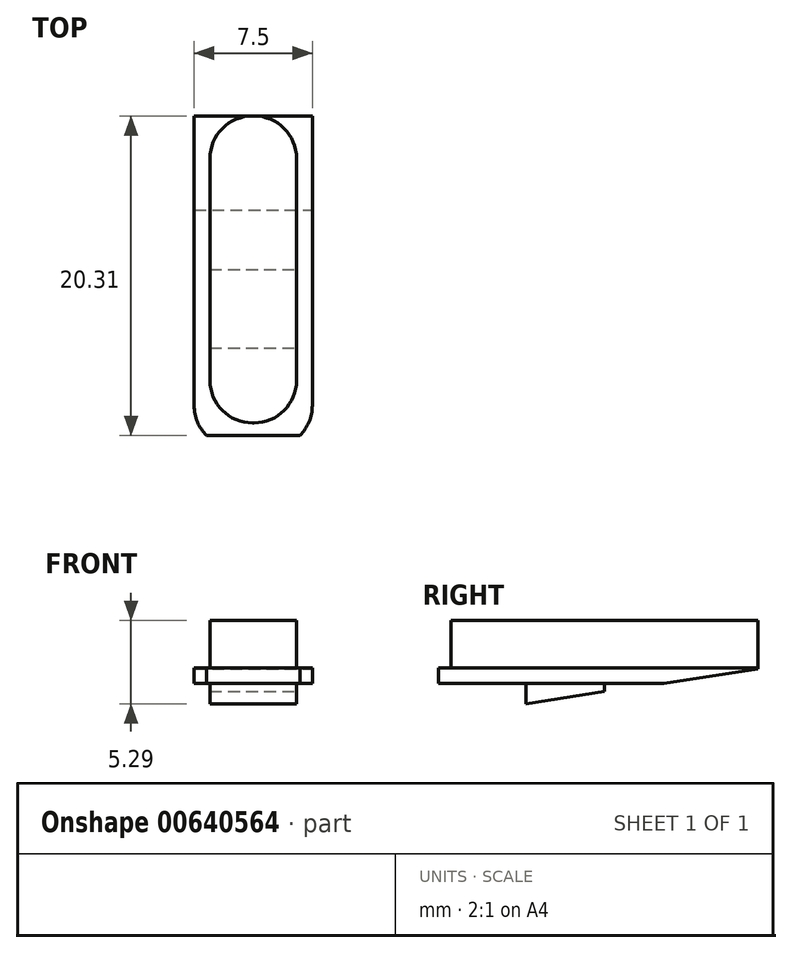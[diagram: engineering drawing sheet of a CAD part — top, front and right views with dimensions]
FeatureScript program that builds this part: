
annotation { "Feature Type Name" : "Feature", "Feature Type Description" : "" }
export const myFeature = defineFeature(function(context is Context, id is Id, definition is map)
    precondition{}
    {
        {
            var Q0;
            Q0=qCreatedBy(makeId("Front.planeOp"),FACE);
            var sketch = newSketch(context, id + "F0", { "sketchPlane" : qUnion([Q0])});
            skLineSegment(sketch, "E0", {"start": v(-5.5, 4) * mm, "end": v(0, 4) * mm});
            skLineSegment(sketch, "E1", {"start": v(0, 4) * mm, "end": v(0, 1) * mm});
            skLineSegment(sketch, "E2", {"start": v(0, 1) * mm, "end": v(1, 1) * mm});
            skLineSegment(sketch, "E3", {"start": v(1, 1) * mm, "end": v(1, 0) * mm});
            skLineSegment(sketch, "E4", {"start": v(1, 0) * mm, "end": v(-6.5, 0) * mm});
            skLineSegment(sketch, "E5", {"start": v(-6.5, 0) * mm, "end": v(-6.5, 1) * mm});
            skLineSegment(sketch, "E6", {"start": v(-6.5, 1) * mm, "end": v(-5.5, 1) * mm});
            skLineSegment(sketch, "E7", {"start": v(-5.5, 1) * mm, "end": v(-5.5, 4) * mm});
            skLineSegment(sketch, "E8", {"start": v(-2.75, 4) * mm, "end": v(-2.75, 8.23) * mm, "construction": true});
            skSolve(sketch);
        }
        {
            var Q0;
            Q0 = qSketchRegion(id + "F0", true);
            extrude(context, id + "F1", {"entities" : qUnion([Q0]), "endBound" : BoundingType.SYMMETRIC, "depth" : 19.5 * mm, "offsetDistance" : 25 * mm});
        }
        {
            var Q0;
            Q0=makeQuery(id+"F1.opExtrude","CAP_FACE",FACE,{"disambiguationData":[OSD([sQuery(id+"F0.wireOp",EDGE,"E0"),sQuery(id+"F0.wireOp",EDGE,"E1"),sQuery(id+"F0.wireOp",EDGE,"E2"),sQuery(id+"F0.wireOp",EDGE,"E3"),sQuery(id+"F0.wireOp",EDGE,"E4"),sQuery(id+"F0.wireOp",EDGE,"E5"),sQuery(id+"F0.wireOp",EDGE,"E6"),sQuery(id+"F0.wireOp",EDGE,"E7")])],"isStart":false});
            var sketch = newSketch(context, id + "F2", { "sketchPlane" : qUnion([Q0])});
            skLineSegment(sketch, "E9.bottom", {"start": v(-6.5, 0) * mm, "end": v(1, 0) * mm});
            skLineSegment(sketch, "E9.top", {"start": v(-6.5, 1) * mm, "end": v(1, 1) * mm});
            skLineSegment(sketch, "E9.left", {"start": v(-6.5, 0) * mm, "end": v(-6.5, 1) * mm});
            skLineSegment(sketch, "E9.right", {"start": v(1, 0) * mm, "end": v(1, 1) * mm});
            skSolve(sketch);
        }
        {
            var Q0;
            Q0 = qSketchRegion(id + "F2", true);
            extrude(context, id + "F3", {"entities" : qUnion([Q0]), "operationType" : NewBodyOperationType.ADD, "depth" : 1.6 * mm, "offsetDistance" : 25 * mm});
        }
        {
            var Q0;
            Q0=makeQuery(id+"F3.opExtrude","CAP_EDGE",EDGE,{"disambiguationData":[OSD([sQuery(id+"F2.wireOp",EDGE,"E9.right")])],"isStart":false});
            var Q1;
            Q1=makeQuery(id+"F3.opExtrude","CAP_EDGE",EDGE,{"disambiguationData":[OSD([sQuery(id+"F2.wireOp",EDGE,"E9.left")])],"isStart":false});
            var Q2;
            Q2=makeQuery(id+"F1.opExtrude","CAP_EDGE",EDGE,{"disambiguationData":[OSD([sQuery(id+"F0.wireOp",EDGE,"E1")])],"isStart":false});
            var Q3;
            Q3=makeQuery(id+"F1.opExtrude","CAP_EDGE",EDGE,{"disambiguationData":[OSD([sQuery(id+"F0.wireOp",EDGE,"E7")])],"isStart":false});
            var Q4;
            Q4=makeQuery(id+"FfYgk94FB1osBZD_1.1.F3.opExtrude","CAP_EDGE",EDGE,{"disambiguationData":[OSD([sQuery(id+"F2.wireOp",EDGE,"E9.right")])],"isStart":false});
            var Q5;
            Q5=makeQuery(id+"F1.opExtrude","CAP_EDGE",EDGE,{"disambiguationData":[OSD([sQuery(id+"F0.wireOp",EDGE,"E1")])],"isStart":true});
            var Q6;
            Q6=makeQuery(id+"FfYgk94FB1osBZD_1.1.F3.opExtrude","CAP_EDGE",EDGE,{"disambiguationData":[OSD([sQuery(id+"F2.wireOp",EDGE,"E9.left")])],"isStart":false});
            var Q7;
            Q7=makeQuery(id+"F1.opExtrude","CAP_EDGE",EDGE,{"disambiguationData":[OSD([sQuery(id+"F0.wireOp",EDGE,"E7")])],"isStart":true});
            fillet(context, id + "F4", {"entities" : qUnion([Q0, Q1, Q2, Q3, Q4, Q5, Q6, Q7]), "radius" : 2.7 * mm, "tangentPropagation" : true, "allowEdgeOverflow" : false});
        }
        {
            var Q0;
            Q0=qCreatedBy(makeId("Right.planeOp"),FACE);
            var sketch = newSketch(context, id + "F5", { "sketchPlane" : qUnion([Q0])});
            skLineSegment(sketch, "E10", {"start": v(-5, 0) * mm, "end": v(-5, -1.3) * mm});
            skLineSegment(sketch, "E11", {"start": v(-5, -1.3) * mm, "end": v(0, -0.5) * mm});
            skLineSegment(sketch, "E12", {"start": v(0, -0.5) * mm, "end": v(0, 0) * mm});
            skLineSegment(sketch, "E13", {"start": v(0, 0) * mm, "end": v(-5, 0) * mm});
            skSolve(sketch);
        }
        {
            var Q0;
            Q0 = qSketchRegion(id + "F5", true);
            var Q1;
            Q1=makeQuery(id+"F1.opExtrude","SWEPT_FACE",FACE,{"disambiguationData":[OSD([sQuery(id+"F0.wireOp",EDGE,"E7")])]});
            extrude(context, id + "F6", {"entities" : qUnion([Q0]), "operationType" : NewBodyOperationType.ADD, "endBound" : BoundingType.UP_TO_SURFACE, "oppositeDirection" : true, "depth" : 5 * mm, "endBoundEntityFace" : qUnion([Q1]), "offsetDistance" : 25 * mm});
        }
        {
            var Q0;
            Q0=qCreatedBy(makeId("Right.planeOp"),FACE);
            var sketch = newSketch(context, id + "F7", { "sketchPlane" : qUnion([Q0])});
            skLineSegment(sketch, "E14", {"start": v(-6.75, -1.67) * mm, "end": v(24.82, 3.33) * mm});
            skLineSegment(sketch, "E15", {"start": v(24.82, 3.33) * mm, "end": v(24.82, -1.67) * mm});
            skLineSegment(sketch, "E16", {"start": v(24.82, -1.67) * mm, "end": v(-6.75, -1.67) * mm});
            skSolve(sketch);
        }
        {
            var Q0;
            Q0 = qSketchRegion(id + "F7", true);
            extrude(context, id + "F8", {"entities" : qUnion([Q0]), "operationType" : NewBodyOperationType.REMOVE, "endBound" : BoundingType.SYMMETRIC, "oppositeDirection" : true, "depth" : 25 * mm, "offsetDistance" : 25 * mm});
        }
        {
            var Q0;
            {var subQ0=sQuery(id+"F2.wireOp",EDGE,"E9.top");Q0=makeQuery(id+"FfYgk94FB1osBZD_1.1.F3.boolean.opBoolean","MERGE",FACE,{"derivedFrom":[makeQuery(id+"F3.boolean.opBoolean","MERGE",FACE,{"derivedFrom":[makeQuery(id+"F1.opExtrude","SWEPT_FACE",FACE,{"disambiguationData":[OSD([sQuery(id+"F0.wireOp",EDGE,"E2")])]}),makeQuery(id+"F1.opExtrude","SWEPT_FACE",FACE,{"disambiguationData":[OSD([sQuery(id+"F0.wireOp",EDGE,"E6")])]}),makeQuery(id+"F3.opExtrude","SWEPT_FACE",FACE,{"disambiguationData":[OSD([subQ0])]})]}),makeQuery(id+"FfYgk94FB1osBZD_1.1.F3.opExtrude","SWEPT_FACE",FACE,{"disambiguationData":[OSD([subQ0])]})]});}
            var sketch = newSketch(context, id + "F9", { "sketchPlane" : qUnion([Q0])});
            skLineSegment(sketch, "E17", {"start": v(-5.7, -10.56) * mm, "end": v(0.2, -10.56) * mm});
            skPoint(sketch, "E17.endSnap0", {"position": v(0.2, -10.56) * mm});
            skArc(sketch, "E18.0", {"start": v(-1.7, -11.35) * mm, "mid": v(-0.67, -11.14) * mm, "end": v(0.2, -10.56) * mm});
            skLineSegment(sketch, "E19.0", {"start": v(-3.8, -11.35) * mm, "end": v(-1.7, -11.35) * mm});
            skArc(sketch, "E19.1", {"start": v(-5.7, -10.56) * mm, "mid": v(-4.83, -11.14) * mm, "end": v(-3.8, -11.35) * mm});
            skPoint(sketch, "E20.orphan", {"position": v(1, -8.65) * mm});
            skPoint(sketch, "E21.orphan", {"position": v(-6.5, -8.65) * mm});
            skSolve(sketch);
        }
        {
            var Q0;
            Q0 = qSketchRegion(id + "F9", true);
            extrude(context, id + "F10", {"entities" : qUnion([Q0]), "operationType" : NewBodyOperationType.REMOVE, "endBound" : BoundingType.THROUGH_ALL, "oppositeDirection" : true, "depth" : 25 * mm, "offsetDistance" : 25 * mm});
        }
    });
